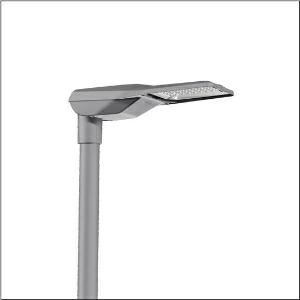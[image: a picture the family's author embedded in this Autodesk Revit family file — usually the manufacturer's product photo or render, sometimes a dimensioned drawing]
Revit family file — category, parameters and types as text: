
# Revit family: streetlight_sl_21_iq_mini___st1_5a_5xe2p31g08gb_08f7
name_source: partatom
category: Lighting Fixtures
units: mm (PartAtom-declared; Revit-internal decimal feet)

## family parameters
Cut with Voids When Loaded = No
Host = Face
Light Source = No
Part Type = Normal
Room Calculation Point = No
Round Connector Dimension = Use Diameter
Shared = No

## types (1)
- --- (1 x LED, 5580 lm, 37.1 W, 3000K)
    Apparent Load = 37 VA
    CIE Flux Codes = 22 53 95 100 100
    Color Rendering = 70
    Color Temperature = 3000K
    Default Elevation = 1800 mm
    Description = Streetlight SL 21 iQ mini, mast luminaire, primary light control with lens, of PMMA, primary optical cover: cover, of toughened safety glass, transparent, light distribution: ST1.5a, light emission: direct distribution, primary light characteristic: asymmetric, installation type: post-top, side-entry, LED, High Power LED, rated luminous flux: 5.580lm, luminous efficacy: 150lm/W, light colour: 730, colour temperature: 3000K, control: Street-Remote, Auto-Match, Temp-Guard, Lumen-Switch, Night-Set, Smart-Wire, Light-Fading, Desk-Remote (wireless, voltage-free reading and setting of iQ features in the workshop via application-optimized NFC function/RFID function), optimised constant luminous flux control (CLO 2.0), pre-setting: linear dimming characteristic, mains connection: 220..240V, AC, 50/60Hz, start of lifetime: 37W, end of service life: 39W, reduction: 18W, luminaire housing, of diecast aluminium, powder-coated, Siteco® metallic grey (DB 702S), corrosivity category C5 mid according to DIN EN ISO 12944, please order mast flange separately, inclination adjustable: 0°, 5°, 10°, 15°, sealing non-destructively replaceable, multi-level sealing system, length: 628mm, width: 235mm, height: 110mm, mast flange for spigot size: 42mm (side-entry): 5XC10008XM4, 60/48mm (side-entry/post-top): 5XC10108XM2, 76/60mm (side-entry/post-top): 5XC10108XM1, protection rating (complete): IP66, insulation class (complete): insulation class II (safety insulation), certification: CE, ENEC, ENEC+, VDE, impact resistance: IK09, permissible operating ambient temperature for outdoor applications: -40..+50°C, standard-compliant lighting for roads and squares, packaging unit: 1 piece

Light Distribution: ST1.5a
    Height = 110 mm
    Lamp = 1 x LED
    Lamp Light Flux = 5580 lm
    Lamp Power = 37.1 W
    Lamp count = 1
    Length = 625 mm
    Luminous efficacy = 150 lm/W
    Manufacturer = Siteco
    ModVariant = No
    Model = 5XE2P31G08GB
    Number of Poles = 1
    OnlyDefault = Yes
    Power Factor = 1
    Product Name = Streetlight SL 21 iQ mini | ST1.5a
    Product group = mast luminaire | pylon top
    ProductGroupID = 6100
    Protection Class = Protection class II
    Protection Degree = IP 66
    RLX_Detail_Level = 1
    RLX_Emergency_Light_Flux = 0 lm
    RLX_Emergency_Type = 0
    RLX_Emergency_Type_DB = No
    RlxData = <blob elided: 96885 chars, md5=d29412ba>
    Socket = socket
    Standby Power = 0 W
    System Light Flux = 5580 lm
    System Power = 37 W
    Type Comments = factory setting: luminous flux: 100 % | dim-lin: 254 | 385 mA
    Type Image = l_1003519.jpg
    URL = http://relux.com
    VarID = @adj_146939
    Voltage = 0 V
    Weight = 0.00 kg
    Width = 234 mm

## geometry (parser evidence)
native form markers: Blend x4, Sweep x11
no freeform markers — native parametric forms only
